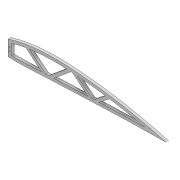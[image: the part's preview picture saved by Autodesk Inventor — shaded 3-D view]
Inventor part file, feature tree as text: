
AUTODESK INVENTOR PART (.ipt)
format: ipt  version: 2022 (Build 260153000, 153)  size: 241,664 bytes
history: native  units: mm
features: extrude x5, sketch x5, projected_geometry x2, shell x1
ambient origin geometry x8: Origin, YZ Plane, XZ Plane, XY Plane, X Axis, Y Axis, Z Axis, Center Point
bodies: Solid1 (feature_tree)
feature tree (13):
  extrude  "Extrusion1"  Depth=5.0mm
  shell  "Shell1"  Thickness=6.0mm
  extrude  "Extrusion2"  Depth=2.0mm
  extrude  "Extrusion3"  Depth=5.9mm
  extrude  "Extrusion4"  Depth=2.3mm
  extrude  "Extrusion5"  Depth=5.0mm TaperAngle=0.0deg
  sketch  "Sketch3"  dims[d0=4.5mm d1=0.0mm d2=5.0mm d3=6.0mm]
  sketch  "Sketch7"  dims[d5=4.5mm d6=0.0mm d7=2.0mm]
  projected_geometry  "Projected Loop3"
  sketch  "Sketch8"  dims[d8=2.0mm d9=5.9mm]
  sketch  "Sketch9"  dims[d10=2.3mm d11=2.3mm]
  sketch  "Sketch10"  dims[d12=4.5mm d13=10.0mm d14=0.0mm d15=25.0mm d16=10.0mm d17=0.0mm d18=5.0mm d19=5.0mm d20=5.0mm d21=5.0mm d22=4.5mm d23=0.0mm]
  projected_geometry  "Projected Loop4"
